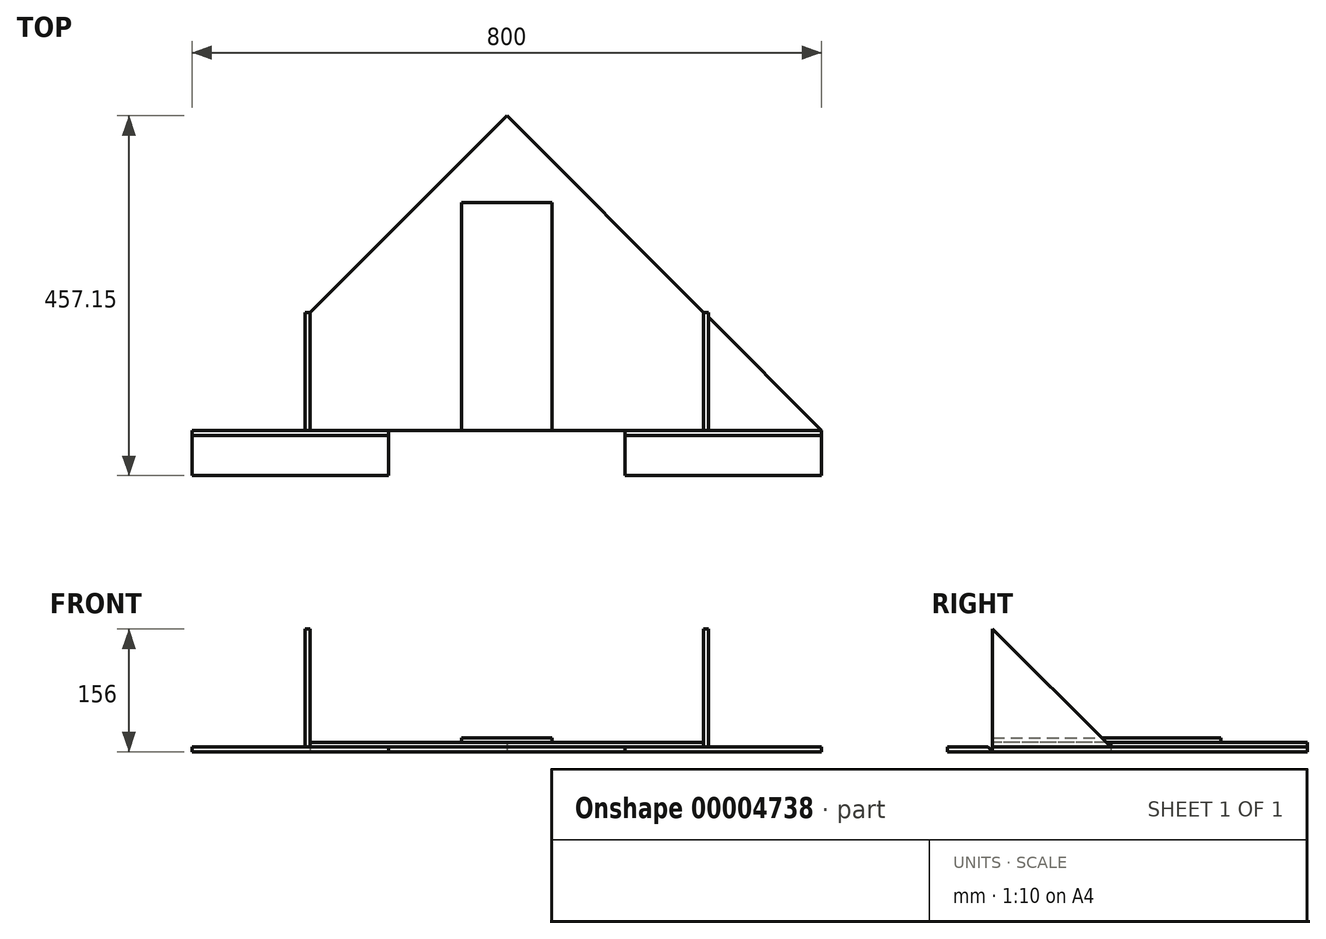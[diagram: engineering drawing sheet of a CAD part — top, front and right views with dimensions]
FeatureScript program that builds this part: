
annotation { "Feature Type Name" : "Feature", "Feature Type Description" : "" }
export const myFeature = defineFeature(function(context is Context, id is Id, definition is map)
    precondition{}
    {
        {
            var Q0;
            Q0=qCreatedBy(makeId("Top.planeOp"),FACE);
            var sketch = newSketch(context, id + "F0", { "sketchPlane" : qUnion([Q0])});
            skLineSegment(sketch, "E0", {"start": v(0, 400) * mm, "end": v(400, 0) * mm});
            skLineSegment(sketch, "E1", {"start": v(400, 0) * mm, "end": v(0, 0) * mm});
            skLineSegment(sketch, "E2", {"start": v(0, 0) * mm, "end": v(0, 400) * mm});
            skLineSegment(sketch, "E3.0.MirrorCS", {"start": v(0, 400) * mm, "end": v(-400, 0) * mm});
            skLineSegment(sketch, "E4.0.MirrorCS", {"start": v(-400, 0) * mm, "end": v(0, 0) * mm});
            skLineSegment(sketch, "E5", {"start": v(-250, 150) * mm, "end": v(-250, 0) * mm});
            skLineSegment(sketch, "E6", {"start": v(-250, 0) * mm, "end": v(0, 0) * mm});
            skLineSegment(sketch, "E7.0.MirrorCS", {"start": v(250, 150) * mm, "end": v(250, 0) * mm});
            skLineSegment(sketch, "E8", {"start": v(-400, 0) * mm, "end": v(-400, -57.15) * mm});
            skLineSegment(sketch, "E9", {"start": v(-400, -57.15) * mm, "end": v(-150, -57.15) * mm});
            skLineSegment(sketch, "E10", {"start": v(-150, -57.15) * mm, "end": v(-150, 0) * mm});
            skLineSegment(sketch, "E11.0.MirrorCS", {"start": v(150, -57.15) * mm, "end": v(150, 0) * mm});
            skLineSegment(sketch, "E11.1.MirrorCS", {"start": v(400, 0) * mm, "end": v(400, -57.15) * mm});
            skLineSegment(sketch, "E11.2.MirrorCS", {"start": v(400, -57.15) * mm, "end": v(150, -57.15) * mm});
            skSolve(sketch);
        }
        {
            var Q0;
            {var subQ0=sQuery(id+"F0.wireOp",EDGE,"E7.0.MirrorCS");Q0=makeQuery(id+"F0.imprint","IMPRINT",FACE,{"disambiguationData":[TD([[makeQuery(id+"F0.imprint","IMPRINT",EDGE,{"derivedFrom":subQ0}),1.0]])]});}
            var Q1;
            {var subQ2=sQuery(id+"F0.wireOp",EDGE,"E2");Q1=makeQuery(id+"F0.imprint","IMPRINT",FACE,{"disambiguationData":[TD([[makeQuery(id+"F0.imprint","IMPRINT",EDGE,{"derivedFrom":subQ2}),1.0]])]});}
            var Q2;
            {var subQ1=sQuery(id+"F0.wireOp",EDGE,"E4.0.MirrorCS");Q2=makeQuery(id+"F0.imprint","IMPRINT",FACE,{"disambiguationData":[TD([[makeQuery(id+"F0.imprint","IMPRINT",EDGE,{"derivedFrom":subQ1}),1.0]])]});}
            var Q3;
            {var subQ0=sQuery(id+"F0.wireOp",EDGE,"E2");Q3=makeQuery(id+"F0.imprint","IMPRINT",FACE,{"disambiguationData":[TD([[makeQuery(id+"F0.imprint","IMPRINT",EDGE,{"derivedFrom":subQ0}),-1.0]])]});}
            extrude(context, id + "F1", {"entities" : qUnion([Q0, Q1, Q2, Q3]), "depth" : 6 * mm});
        }
        {
            var Q0;
            {var subQ0=sQuery(id+"F0.wireOp",EDGE,"E2");Q0=makeQuery(id+"F0.imprint","IMPRINT",FACE,{"disambiguationData":[TD([[makeQuery(id+"F0.imprint","IMPRINT",EDGE,{"derivedFrom":subQ0}),-1.0]])]});}
            var Q1;
            {var subQ2=sQuery(id+"F0.wireOp",EDGE,"E2");Q1=makeQuery(id+"F0.imprint","IMPRINT",FACE,{"disambiguationData":[TD([[makeQuery(id+"F0.imprint","IMPRINT",EDGE,{"derivedFrom":subQ2}),1.0]])]});}
            extrude(context, id + "F2", {"entities" : qUnion([Q0, Q1]), "depth" : 6 * mm});
        }
        {
            var Q0;
            Q0=makeQuery(id+"F2.opExtrude","SWEPT_BODY",BODY,{"disambiguationData":[OSD([sQuery(id+"F0.wireOp",EDGE,"E0"),sQuery(id+"F0.wireOp",EDGE,"E1"),sQuery(id+"F0.wireOp",EDGE,"E3.0.MirrorCS"),sQuery(id+"F0.wireOp",EDGE,"E5"),sQuery(id+"F0.wireOp",EDGE,"E6"),sQuery(id+"F0.wireOp",EDGE,"E7.0.MirrorCS")])]});
            transform(context, id + "F3", {"entities" : qUnion([Q0]), "transformType" : TransformType.TRANSLATION_3D, "dx" : 0 * mm, "dy" : 0 * mm, "dz" : 6 * mm, "makeCopy" : false});
        }
        {
            var Q0;
            {var subQ0=sQuery(id+"F0.wireOp",EDGE,"E7.0.MirrorCS");Q0=makeQuery(id+"F0.imprint","IMPRINT",FACE,{"disambiguationData":[TD([[makeQuery(id+"F0.imprint","IMPRINT",EDGE,{"derivedFrom":subQ0}),1.0]])]});}
            extrude(context, id + "F4", {"entities" : qUnion([Q0]), "depth" : 6 * mm});
        }
        {
            var Q0;
            Q0=makeQuery(id+"F4.opExtrude","SWEPT_BODY",BODY,{"disambiguationData":[OSD([sQuery(id+"F0.wireOp",EDGE,"E0"),sQuery(id+"F0.wireOp",EDGE,"E1"),sQuery(id+"F0.wireOp",EDGE,"E7.0.MirrorCS")])]});
            var Q1;
            Q1=sQuery(id+"F0.wireOp",EDGE,"E7.0.MirrorCS");
            transform(context, id + "F5", {"entities" : qUnion([Q0]), "transformType" : TransformType.ROTATION, "transformAxis" : qUnion([Q1]), "angle" : 90 * degree, "makeCopy" : false});
        }
        {
            var Q0;
            Q0=makeQuery(id+"F4.opExtrude","SWEPT_BODY",BODY,{"disambiguationData":[OSD([sQuery(id+"F0.wireOp",EDGE,"E0"),sQuery(id+"F0.wireOp",EDGE,"E1"),sQuery(id+"F0.wireOp",EDGE,"E7.0.MirrorCS")])]});
            transform(context, id + "F6", {"entities" : qUnion([Q0]), "transformType" : TransformType.TRANSLATION_3D, "dx" : 6 * mm, "dy" : 0 * mm, "dz" : 6 * mm, "makeCopy" : false});
        }
        {
            var Q0;
            Q0=makeQuery(id+"F4.opExtrude","SWEPT_BODY",BODY,{"disambiguationData":[OSD([sQuery(id+"F0.wireOp",EDGE,"E0"),sQuery(id+"F0.wireOp",EDGE,"E1"),sQuery(id+"F0.wireOp",EDGE,"E7.0.MirrorCS")])]});
            var Q1;
            Q1=qCreatedBy(makeId("Right.planeOp"),FACE);
            mirror(context, id + "F7", {"entities" : qUnion([Q0]), "mirrorPlane" : qUnion([Q1])});
        }
        {
            var Q0;
            {var subQ2=sQuery(id+"F0.wireOp",EDGE,"E4.0.MirrorCS");Q0=makeQuery(id+"F0.imprint","IMPRINT",FACE,{"disambiguationData":[TD([[makeQuery(id+"F0.imprint","IMPRINT",EDGE,{"derivedFrom":subQ2}),-1.0]])]});}
            var Q1;
            {var subQ1=sQuery(id+"F0.wireOp",EDGE,"E11.0.MirrorCS");Q1=makeQuery(id+"F0.imprint","IMPRINT",FACE,{"disambiguationData":[TD([[makeQuery(id+"F0.imprint","IMPRINT",EDGE,{"derivedFrom":subQ1}),-1.0]])]});}
            extrude(context, id + "F8", {"entities" : qUnion([Q0, Q1]), "depth" : 6 * mm});
        }
        {
            var Q0;
            Q0=makeQuery(id+"F8.opExtrude","CAP_EDGE",EDGE,{"disambiguationData":[OSD([sQuery(id+"F0.wireOp",EDGE,"E1")])],"isStart":false});
            chamfer(context, id + "F9", {"entities" : qUnion([Q0]), "width" : 6 * mm, "tangentPropagation" : true});
        }
        {
            var Q0;
            Q0=makeQuery(id+"F8.opExtrude","CAP_EDGE",EDGE,{"disambiguationData":[OSD([sQuery(id+"F0.wireOp",EDGE,"E4.0.MirrorCS"),sQuery(id+"F0.wireOp",EDGE,"E6")])],"isStart":false});
            chamfer(context, id + "F10", {"entities" : qUnion([Q0]), "width" : 6 * mm, "tangentPropagation" : true});
        }
        {
            var Q0;
            Q0=qCreatedBy(makeId("Top.planeOp"),FACE);
            var sketch = newSketch(context, id + "F11", { "sketchPlane" : qUnion([Q0])});
            skLineSegment(sketch, "E12", {"start": v(0, 0) * mm, "end": v(57.31, 0) * mm});
            skLineSegment(sketch, "E13", {"start": v(57.31, 0) * mm, "end": v(57.31, 289.95) * mm});
            skLineSegment(sketch, "E14", {"start": v(57.31, 289.95) * mm, "end": v(0, 289.95) * mm});
            skLineSegment(sketch, "E15", {"start": v(57.31, 0) * mm, "end": v(0, 0) * mm});
            skLineSegment(sketch, "E16.0.MirrorCS", {"start": v(0, 0) * mm, "end": v(-57.31, 0) * mm});
            skLineSegment(sketch, "E16.1.MirrorCS", {"start": v(-57.31, 289.95) * mm, "end": v(0, 289.95) * mm});
            skLineSegment(sketch, "E16.2.MirrorCS", {"start": v(-57.31, 0) * mm, "end": v(-57.31, 289.95) * mm});
            skSolve(sketch);
        }
        {
            var Q0;
            Q0 = qSketchRegion(id + "F11", true);
            extrude(context, id + "F12", {"entities" : qUnion([Q0]), "oppositeDirection" : true, "depth" : 6 * mm});
        }
        {
            var Q0;
            Q0=makeQuery(id+"F12.opExtrude","SWEPT_BODY",BODY,{"disambiguationData":[OSD([sQuery(id+"F11.wireOp",EDGE,"E13"),sQuery(id+"F11.wireOp",EDGE,"E14"),sQuery(id+"F11.wireOp",EDGE,"E15"),sQuery(id+"F11.wireOp",EDGE,"E16.2.MirrorCS")])]});
            transform(context, id + "F13", {"entities" : qUnion([Q0]), "transformType" : TransformType.TRANSLATION_3D, "dx" : 0 * mm, "dy" : 0 * mm, "dz" : 18 * mm, "makeCopy" : false});
        }
    });
